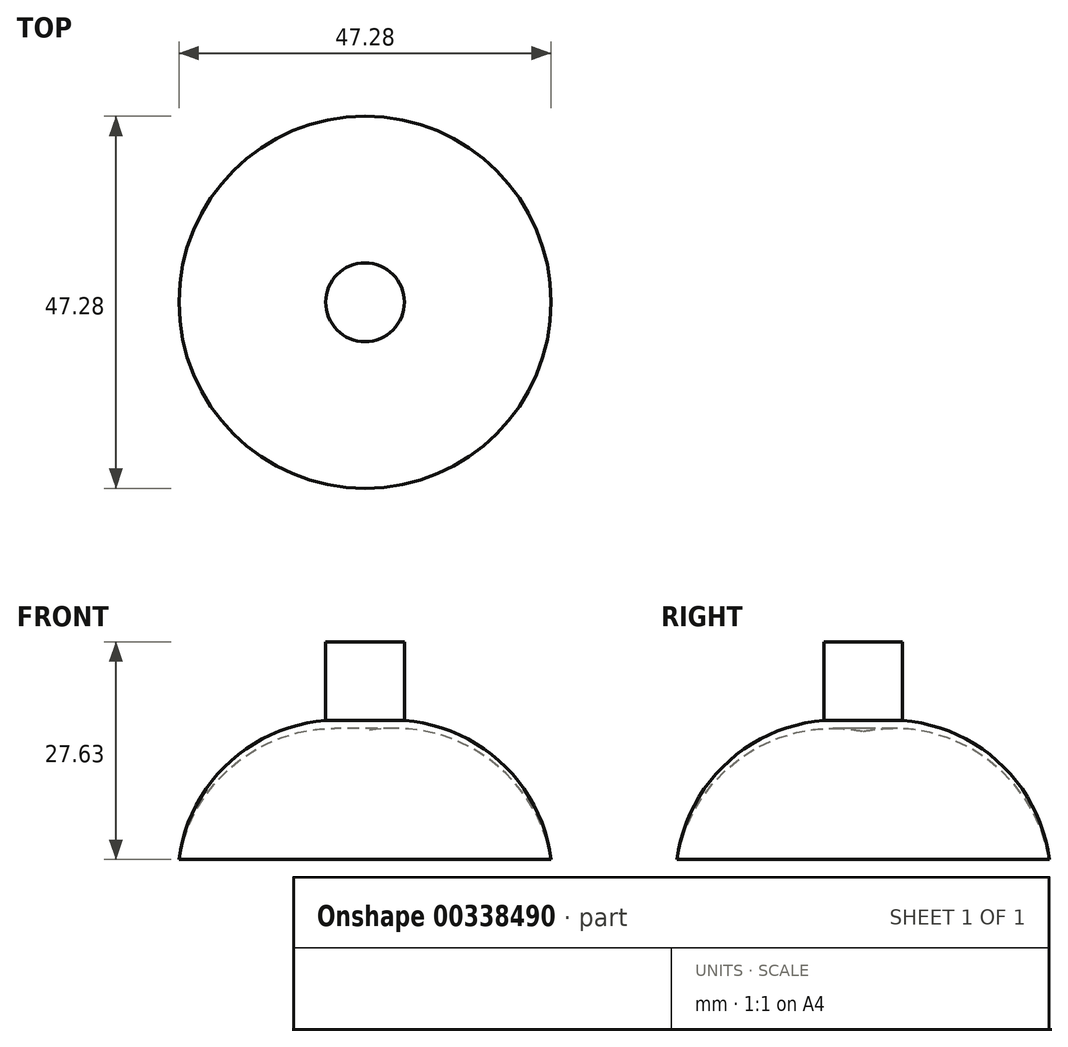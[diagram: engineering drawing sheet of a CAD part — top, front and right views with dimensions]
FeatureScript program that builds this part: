
annotation { "Feature Type Name" : "Feature", "Feature Type Description" : "" }
export const myFeature = defineFeature(function(context is Context, id is Id, definition is map)
    precondition{}
    {
        {
            var Q0;
            Q0=qCreatedBy(makeId("Front.planeOp"),FACE);
            var sketch = newSketch(context, id + "F0", { "sketchPlane" : qUnion([Q0])});
            skLineSegment(sketch, "E0", {"start": v(-5, 27.63) * mm, "end": v(0, 27.63) * mm});
            skLineSegment(sketch, "E1", {"start": v(-5, 27.63) * mm, "end": v(-5, 17.63) * mm});
            skArc(sketch, "E2", {"start": v(-23.64, 0) * mm, "mid": v(-17.9, -17.78) * mm, "end": v(0, -23.14) * mm});
            skArc(sketch, "E3", {"start": v(-5, 17.63) * mm, "mid": v(-17.45, 12.13) * mm, "end": v(-23.64, 0) * mm});
            skLineSegment(sketch, "E4", {"start": v(0, 27.63) * mm, "end": v(0, -23.14) * mm});
            skLineSegment(sketch, "E5", {"start": v(0, 27.63) * mm, "end": v(0, -23.14) * mm, "construction": true});
            skSolve(sketch);
        }
        {
            var Q0;
            Q0=makeQuery(id+"F0.imprint","IMPRINT",FACE,{"disambiguationData":[TD([[makeQuery(id+"F0.imprint","IMPRINT",EDGE,{"derivedFrom":sQuery(id+"F0.wireOp",EDGE,"E0")}),-1.0]])]});
            var Q1;
            Q1=sQuery(id+"F0.wireOp",EDGE,"E4");
            revolve(context, id + "F1", {"entities" : qUnion([Q0]), "axis" : qUnion([Q1]), "revolveType" : RevolveType.FULL});
        }
    });
